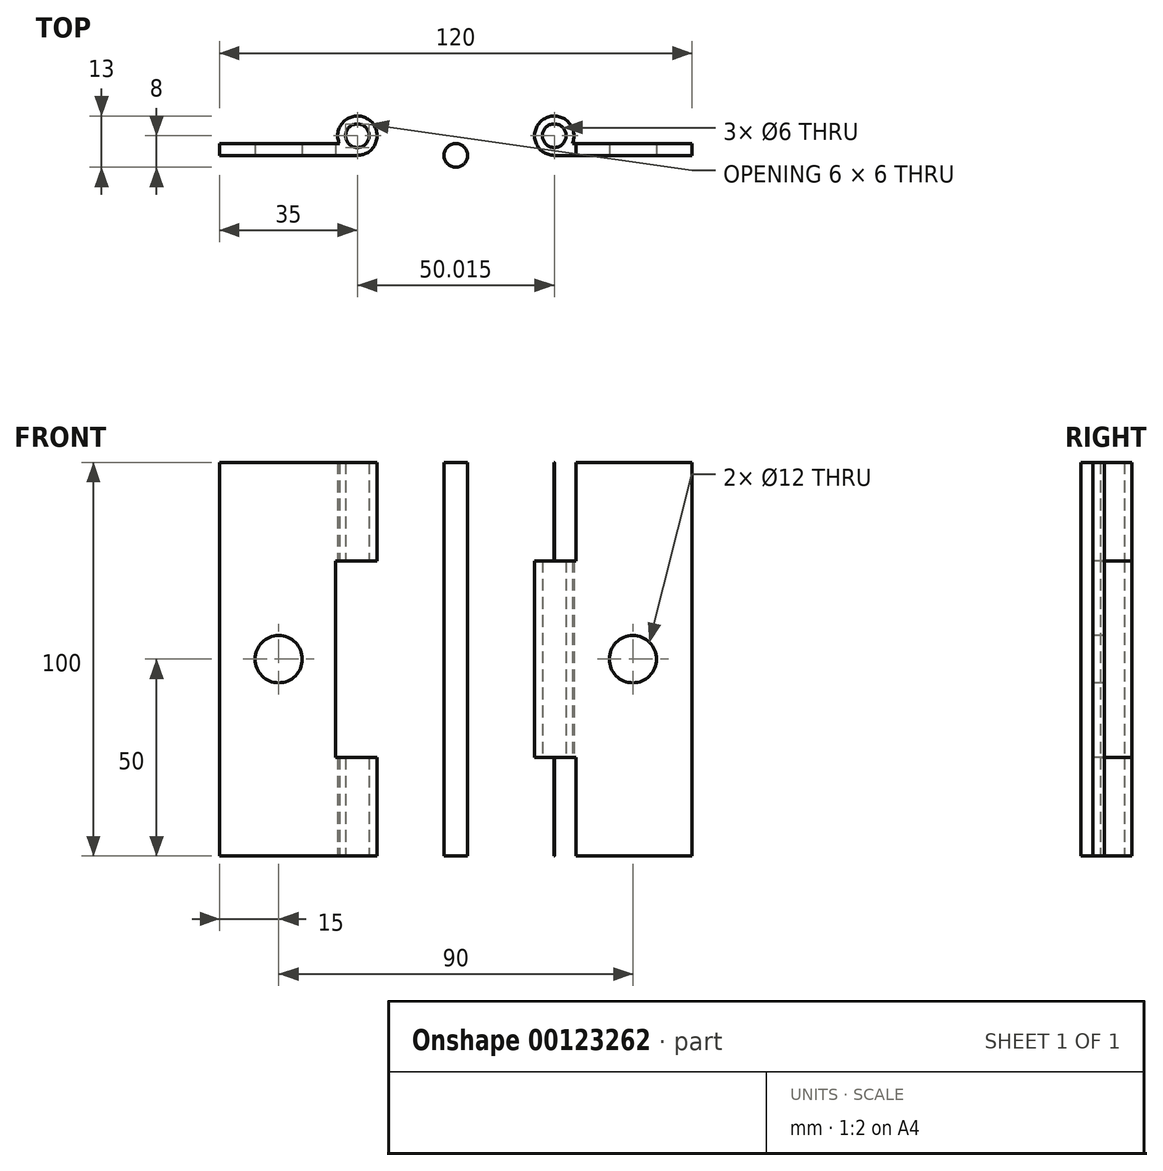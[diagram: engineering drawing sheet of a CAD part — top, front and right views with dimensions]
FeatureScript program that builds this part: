
annotation { "Feature Type Name" : "Feature", "Feature Type Description" : "" }
export const myFeature = defineFeature(function(context is Context, id is Id, definition is map)
    precondition{}
    {
        {
            var Q0;
            Q0=qCreatedBy(makeId("Front.planeOp"),FACE);
            var sketch = newSketch(context, id + "F0", { "sketchPlane" : qUnion([Q0])});
            skLineSegment(sketch, "E0.bottom", {"start": v(-35, 50) * mm, "end": v(0, 50) * mm});
            skLineSegment(sketch, "E0.top", {"start": v(-35, -50) * mm, "end": v(0, -50) * mm});
            skLineSegment(sketch, "E0.left", {"start": v(-35, 50) * mm, "end": v(-35, -50) * mm});
            skLineSegment(sketch, "E0.right", {"start": v(0, 50) * mm, "end": v(0, -50) * mm});
            skCircle(sketch, "E1", {"center": v(-20, 0) * mm, "radius": 6 * mm});
            skLineSegment(sketch, "E2.bottom", {"start": v(-5.5, 25) * mm, "end": v(5.5, 25) * mm});
            skLineSegment(sketch, "E2.top", {"start": v(-5.5, -25) * mm, "end": v(5.5, -25) * mm});
            skLineSegment(sketch, "E2.left", {"start": v(-5.5, 25) * mm, "end": v(-5.5, -25) * mm});
            skLineSegment(sketch, "E2.right", {"start": v(5.5, 25) * mm, "end": v(5.5, -25) * mm});
            skSolve(sketch);
        }
        {
            var Q0;
            Q0=qCreatedBy(makeId("Top.planeOp"),FACE);
            var sketch = newSketch(context, id + "F1", { "sketchPlane" : qUnion([Q0])});
            skCircle(sketch, "E3", {"center": v(0, 5) * mm, "radius": 5 * mm});
            skCircle(sketch, "E4", {"center": v(0, 5) * mm, "radius": 3 * mm});
            skSolve(sketch);
        }
        {
            var Q0;
            Q0=makeQuery(id+"F1.imprint","IMPRINT",FACE,{"disambiguationData":[TD([[makeQuery(id+"F1.imprint","IMPRINT",EDGE,{"derivedFrom":sQuery(id+"F1.wireOp",EDGE,"E3")}),1.0]])]});
            extrude(context, id + "F2", {"entities" : qUnion([Q0]), "endBound" : BoundingType.SYMMETRIC, "depth" : 100 * mm});
        }
        {
            var Q0;
            Q0=qCreatedBy(makeId("Right.planeOp"),FACE);
            cPlane(context, id + "F3", {"entities" : qUnion([Q0]), "cplaneType" : CPlaneType.OFFSET, "offset" : 35 * mm, "oppositeDirection" : true, "width" : 150 * mm, "height" : 150 * mm});
        }
        {
            var Q0;
            Q0=qCreatedBy(id+"F3.planeOp",FACE);
            var sketch = newSketch(context, id + "F4", { "sketchPlane" : qUnion([Q0])});
            skLineSegment(sketch, "E5.bottom", {"start": v(3, -50) * mm, "end": v(0, -50) * mm});
            skLineSegment(sketch, "E5.top", {"start": v(3, 50) * mm, "end": v(0, 50) * mm});
            skLineSegment(sketch, "E5.left", {"start": v(3, -50) * mm, "end": v(3, 50) * mm});
            skLineSegment(sketch, "E5.right", {"start": v(0, -50) * mm, "end": v(0, 50) * mm});
            skSolve(sketch);
        }
        {
            var Q0;
            Q0=makeQuery(id+"F4.imprint","IMPRINT",FACE,{"disambiguationData":[TD([[makeQuery(id+"F4.imprint","IMPRINT",EDGE,{"derivedFrom":sQuery(id+"F4.wireOp",EDGE,"E5.bottom")}),-1.0]])]});
            extrude(context, id + "F5", {"entities" : qUnion([Q0]), "operationType" : NewBodyOperationType.ADD, "endBound" : BoundingType.UP_TO_NEXT, "depth" : 25 * mm});
        }
        {
            var Q0;
            Q0=makeQuery(id+"F0.imprint","IMPRINT",FACE,{"disambiguationData":[TD([[makeQuery(id+"F0.imprint","IMPRINT",EDGE,{"derivedFrom":sQuery(id+"F0.wireOp",EDGE,"E1")}),1.0]])]});
            var Q1;
            Q1=makeQuery(id+"F5.opExtrude","SWEPT_FACE",FACE,{"disambiguationData":[OSD([sQuery(id+"F4.wireOp",EDGE,"E5.left")])]});
            extrude(context, id + "F6", {"entities" : qUnion([Q0]), "operationType" : NewBodyOperationType.REMOVE, "endBound" : BoundingType.UP_TO_SURFACE, "oppositeDirection" : true, "endBoundEntityFace" : qUnion([Q1]), "depth" : 25 * mm});
        }
        {
            var Q0;
            {var subQ5=sQuery(id+"F0.wireOp",EDGE,"E2.right");Q0=makeQuery(id+"F0.imprint","IMPRINT",FACE,{"disambiguationData":[TD([[makeQuery(id+"F0.imprint","IMPRINT",EDGE,{"derivedFrom":subQ5}),-1.0]])]});}
            var Q1;
            {var subQ5=sQuery(id+"F0.wireOp",EDGE,"E2.left");Q1=makeQuery(id+"F0.imprint","IMPRINT",FACE,{"disambiguationData":[TD([[makeQuery(id+"F0.imprint","IMPRINT",EDGE,{"derivedFrom":subQ5}),1.0]])]});}
            extrude(context, id + "F7", {"entities" : qUnion([Q0, Q1]), "operationType" : NewBodyOperationType.REMOVE, "oppositeDirection" : true, "depth" : 11 * mm});
        }
        {
            var Q0;
            Q0=qCreatedBy(makeId("Right.planeOp"),FACE);
            cPlane(context, id + "F8", {"entities" : qUnion([Q0]), "cplaneType" : CPlaneType.OFFSET, "offset" : 50 * mm, "width" : 150 * mm, "height" : 150 * mm});
        }
        {
            var Q0;
            Q0=qCreatedBy(makeId("Front.planeOp"),FACE);
            var sketch = newSketch(context, id + "F9", { "sketchPlane" : qUnion([Q0])});
            skLineSegment(sketch, "E6.bottom", {"start": v(50, 50) * mm, "end": v(85, 50) * mm});
            skLineSegment(sketch, "E6.top", {"start": v(50, -50) * mm, "end": v(85, -50) * mm});
            skLineSegment(sketch, "E6.left", {"start": v(50, 50) * mm, "end": v(50, -50) * mm});
            skLineSegment(sketch, "E6.right", {"start": v(85, 50) * mm, "end": v(85, -50) * mm});
            skCircle(sketch, "E7", {"center": v(70, 0) * mm, "radius": 6 * mm});
            skLineSegment(sketch, "E8.bottom", {"start": v(55.5, 50) * mm, "end": v(44.5, 50) * mm});
            skLineSegment(sketch, "E8.top", {"start": v(55.5, 25) * mm, "end": v(44.5, 25) * mm});
            skLineSegment(sketch, "E8.left", {"start": v(55.5, 50) * mm, "end": v(55.5, 25) * mm});
            skLineSegment(sketch, "E8.right", {"start": v(44.5, 50) * mm, "end": v(44.5, 25) * mm});
            skLineSegment(sketch, "E9.MirrorCS", {"start": v(55.5, -50) * mm, "end": v(55.5, -25) * mm});
            skLineSegment(sketch, "E10.MirrorCS", {"start": v(44.5, -50) * mm, "end": v(44.5, -25) * mm});
            skLineSegment(sketch, "E11.MirrorCS", {"start": v(55.5, -25) * mm, "end": v(44.5, -25) * mm});
            skLineSegment(sketch, "E12.MirrorCS", {"start": v(55.5, -50) * mm, "end": v(44.5, -50) * mm});
            skSolve(sketch);
        }
        {
            var Q0;
            Q0=qCreatedBy(makeId("Top.planeOp"),FACE);
            var sketch = newSketch(context, id + "F10", { "sketchPlane" : qUnion([Q0])});
            skCircle(sketch, "E13", {"center": v(50.02, 5) * mm, "radius": 5 * mm});
            skCircle(sketch, "E14", {"center": v(50.02, 5) * mm, "radius": 3 * mm});
            skSolve(sketch);
        }
        {
            var Q0;
            Q0=makeQuery(id+"F10.imprint","IMPRINT",FACE,{"disambiguationData":[TD([[makeQuery(id+"F10.imprint","IMPRINT",EDGE,{"derivedFrom":sQuery(id+"F10.wireOp",EDGE,"E13")}),1.0]])]});
            extrude(context, id + "F11", {"entities" : qUnion([Q0]), "endBound" : BoundingType.SYMMETRIC, "depth" : 100 * mm});
        }
        {
            var Q0;
            Q0=qCreatedBy(id+"F8.planeOp",FACE);
            cPlane(context, id + "F12", {"entities" : qUnion([Q0]), "cplaneType" : CPlaneType.OFFSET, "offset" : 35 * mm, "width" : 150 * mm, "height" : 150 * mm});
        }
        {
            var Q0;
            Q0=qCreatedBy(id+"F12.planeOp",FACE);
            var sketch = newSketch(context, id + "F13", { "sketchPlane" : qUnion([Q0])});
            skLineSegment(sketch, "E15.bottom", {"start": v(0, -50) * mm, "end": v(3, -50) * mm});
            skLineSegment(sketch, "E15.top", {"start": v(0, 50) * mm, "end": v(3, 50) * mm});
            skLineSegment(sketch, "E15.left", {"start": v(0, -50) * mm, "end": v(0, 50) * mm});
            skLineSegment(sketch, "E15.right", {"start": v(3, -50) * mm, "end": v(3, 50) * mm});
            skSolve(sketch);
        }
        {
            var Q0;
            Q0=makeQuery(id+"F13.imprint","IMPRINT",FACE,{"disambiguationData":[TD([[makeQuery(id+"F13.imprint","IMPRINT",EDGE,{"derivedFrom":sQuery(id+"F13.wireOp",EDGE,"E15.bottom")}),1.0]])]});
            var Q1;
            Q1=makeQuery(id+"F11.opExtrude","SWEPT_FACE",FACE,{"disambiguationData":[OSD([sQuery(id+"F10.wireOp",EDGE,"E13")])]});
            extrude(context, id + "F14", {"entities" : qUnion([Q0]), "operationType" : NewBodyOperationType.ADD, "endBound" : BoundingType.UP_TO_SURFACE, "oppositeDirection" : true, "endBoundEntityFace" : qUnion([Q1]), "depth" : 25 * mm});
        }
        {
            var Q0;
            Q0=makeQuery(id+"F9.imprint","IMPRINT",FACE,{"disambiguationData":[TD([[makeQuery(id+"F9.imprint","IMPRINT",EDGE,{"derivedFrom":sQuery(id+"F9.wireOp",EDGE,"E7")}),1.0]])]});
            var Q1;
            Q1=makeQuery(id+"F14.opExtrude","SWEPT_FACE",FACE,{"disambiguationData":[OSD([sQuery(id+"F13.wireOp",EDGE,"E15.right")])]});
            extrude(context, id + "F15", {"entities" : qUnion([Q0]), "operationType" : NewBodyOperationType.REMOVE, "endBound" : BoundingType.UP_TO_SURFACE, "oppositeDirection" : true, "endBoundEntityFace" : qUnion([Q1]), "depth" : 25 * mm});
        }
        {
            var Q0;
            {var subQ5=sQuery(id+"F9.wireOp",EDGE,"E10.MirrorCS");Q0=makeQuery(id+"F9.imprint","IMPRINT",FACE,{"disambiguationData":[TD([[makeQuery(id+"F9.imprint","IMPRINT",EDGE,{"derivedFrom":subQ5}),-1.0]])]});}
            var Q1;
            {var subQ5=sQuery(id+"F9.wireOp",EDGE,"E8.right");Q1=makeQuery(id+"F9.imprint","IMPRINT",FACE,{"disambiguationData":[TD([[makeQuery(id+"F9.imprint","IMPRINT",EDGE,{"derivedFrom":subQ5}),1.0]])]});}
            var Q2;
            {var subQ5=sQuery(id+"F9.wireOp",EDGE,"E8.left");Q2=makeQuery(id+"F9.imprint","IMPRINT",FACE,{"disambiguationData":[TD([[makeQuery(id+"F9.imprint","IMPRINT",EDGE,{"derivedFrom":subQ5}),-1.0]])]});}
            var Q3;
            {var subQ5=sQuery(id+"F9.wireOp",EDGE,"E9.MirrorCS");Q3=makeQuery(id+"F9.imprint","IMPRINT",FACE,{"disambiguationData":[TD([[makeQuery(id+"F9.imprint","IMPRINT",EDGE,{"derivedFrom":subQ5}),1.0]])]});}
            extrude(context, id + "F16", {"entities" : qUnion([Q0, Q1, Q2, Q3]), "operationType" : NewBodyOperationType.REMOVE, "oppositeDirection" : true, "depth" : 11 * mm});
        }
        {
            var Q0;
            Q0=qCreatedBy(makeId("Right.planeOp"),FACE);
            cPlane(context, id + "F17", {"entities" : qUnion([Q0]), "cplaneType" : CPlaneType.OFFSET, "offset" : 25 * mm, "width" : 150 * mm, "height" : 150 * mm});
        }
        {
            var Q0;
            Q0=qCreatedBy(makeId("Top.planeOp"),FACE);
            var sketch = newSketch(context, id + "F18", { "sketchPlane" : qUnion([Q0])});
            skCircle(sketch, "E16", {"center": v(25, 0) * mm, "radius": 3 * mm});
            skSolve(sketch);
        }
        {
            var Q0;
            Q0=makeQuery(id+"F18.imprint","IMPRINT",FACE,{"disambiguationData":[TD([[makeQuery(id+"F18.imprint","IMPRINT",EDGE,{"derivedFrom":sQuery(id+"F18.wireOp",EDGE,"E16")}),1.0]])]});
            extrude(context, id + "F19", {"entities" : qUnion([Q0]), "endBound" : BoundingType.SYMMETRIC, "depth" : 100 * mm});
        }
    });
